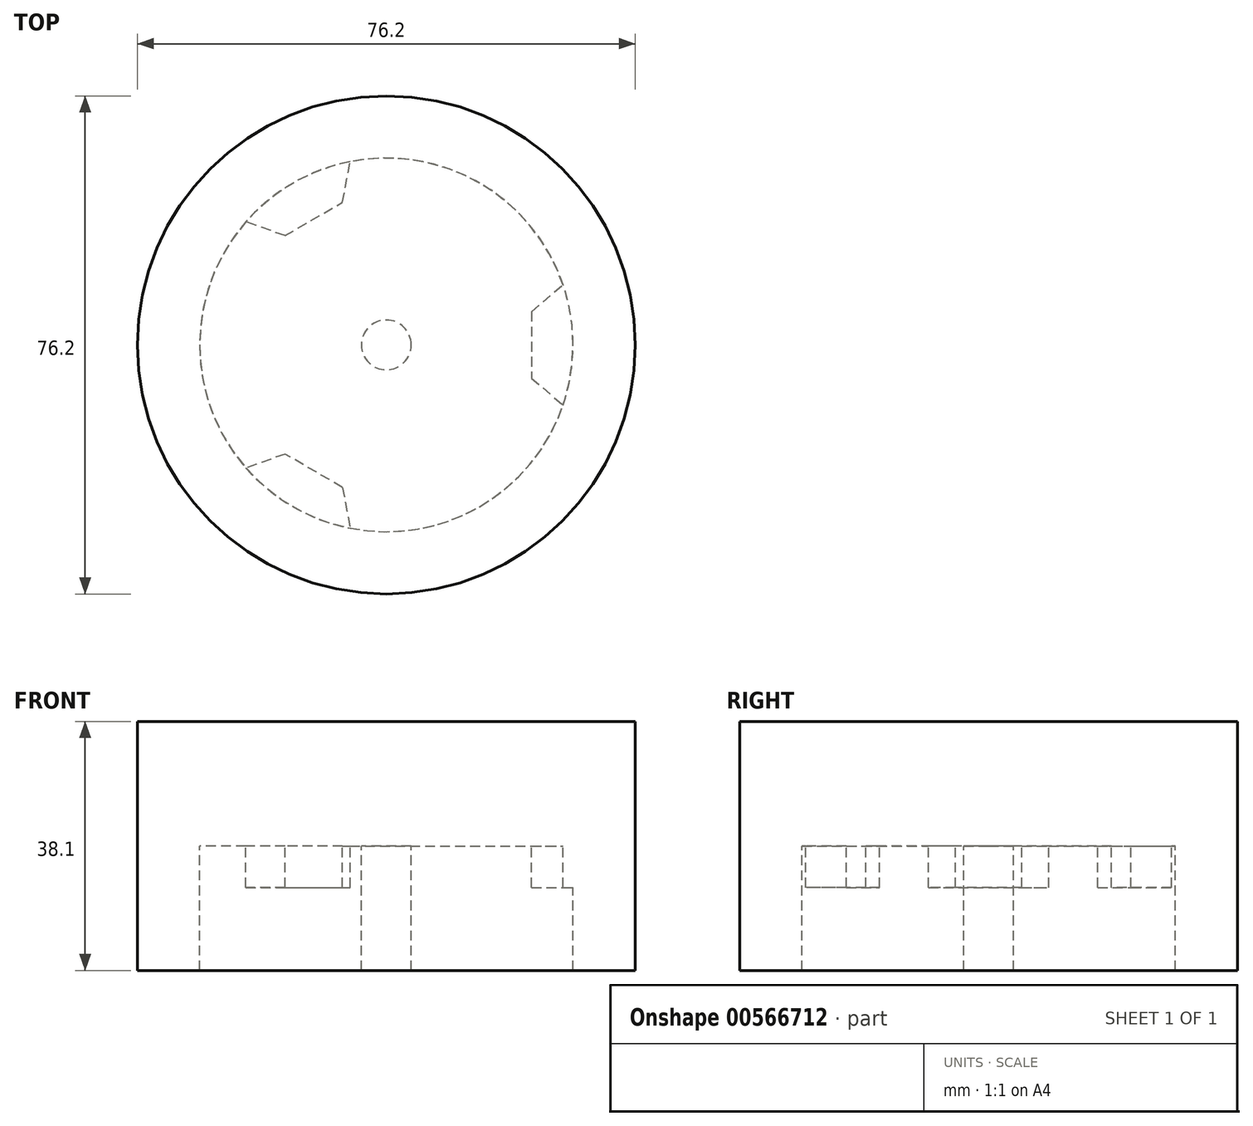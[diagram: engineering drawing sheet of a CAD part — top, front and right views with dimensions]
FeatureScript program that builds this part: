
annotation { "Feature Type Name" : "Feature", "Feature Type Description" : "" }
export const myFeature = defineFeature(function(context is Context, id is Id, definition is map)
    precondition{}
    {
        {
            var Q0;
            Q0=qCreatedBy(makeId("Front.planeOp"),FACE);
            var sketch = newSketch(context, id + "F0", { "sketchPlane" : qUnion([Q0])});
            skLineSegment(sketch, "E0", {"start": v(0, 0) * mm, "end": v(28.58, 0) * mm});
            skLineSegment(sketch, "E1", {"start": v(28.58, 0) * mm, "end": v(28.58, -19.05) * mm});
            skLineSegment(sketch, "E2", {"start": v(28.58, -19.05) * mm, "end": v(38.1, -19.05) * mm});
            skLineSegment(sketch, "E3", {"start": v(38.1, -19.05) * mm, "end": v(38.1, 19.05) * mm});
            skLineSegment(sketch, "E4", {"start": v(38.1, 19.05) * mm, "end": v(0, 19.05) * mm});
            skLineSegment(sketch, "E5", {"start": v(0, 19.05) * mm, "end": v(0, 0) * mm});
            skLineSegment(sketch, "E6", {"start": v(0, 0) * mm, "end": v(0, -19.05) * mm});
            skLineSegment(sketch, "E7", {"start": v(0, -19.05) * mm, "end": v(3.81, -19.05) * mm});
            skLineSegment(sketch, "E8", {"start": v(3.81, -19.05) * mm, "end": v(3.81, 0) * mm});
            skSolve(sketch);
        }
        {
            var Q0;
            Q0 = qSketchRegion(id + "F0", true);
            var Q1;
            Q1=sQuery(id+"F0.wireOp",EDGE,"E5");
            revolve(context, id + "F1", {"entities" : qUnion([Q0]), "axis" : qUnion([Q1]), "revolveType" : RevolveType.FULL});
        }
        {
            var Q0;
            Q0=makeQuery(id+"F1.opRevolve","SWEPT_FACE",FACE,{"disambiguationData":[OSD([sQuery(id+"F0.wireOp",EDGE,"E0")])]});
            var sketch = newSketch(context, id + "F2", { "sketchPlane" : qUnion([Q0])});
            skLineSegment(sketch, "E9", {"start": v(28.58, 0) * mm, "end": v(22.23, 0) * mm});
            skLineSegment(sketch, "E10", {"start": v(22.23, 0) * mm, "end": v(22.23, 5.08) * mm});
            skLineSegment(sketch, "E11", {"start": v(22.23, 5.08) * mm, "end": v(27.05, 9.2) * mm});
            skLineSegment(sketch, "E12", {"start": v(22.23, 0) * mm, "end": v(22.23, -5.08) * mm});
            skLineSegment(sketch, "E13", {"start": v(22.23, -5.08) * mm, "end": v(27.05, -9.2) * mm});
            skLineSegment(sketch, "E14.1.0", {"start": v(-11.11, -19.25) * mm, "end": v(-6.71, -21.79) * mm});
            skLineSegment(sketch, "E14.1.1", {"start": v(-11.11, -19.25) * mm, "end": v(-15.51, -16.7) * mm});
            skLineSegment(sketch, "E14.1.2", {"start": v(-6.71, -21.79) * mm, "end": v(-5.55, -28.03) * mm});
            skLineSegment(sketch, "E14.1.3", {"start": v(-15.51, -16.7) * mm, "end": v(-21.5, -18.82) * mm});
            skLineSegment(sketch, "E14.2.0", {"start": v(-11.11, 19.25) * mm, "end": v(-15.51, 16.7) * mm});
            skLineSegment(sketch, "E14.2.1", {"start": v(-11.11, 19.25) * mm, "end": v(-6.71, 21.79) * mm});
            skLineSegment(sketch, "E14.2.2", {"start": v(-15.51, 16.7) * mm, "end": v(-21.5, 18.82) * mm});
            skLineSegment(sketch, "E14.2.3", {"start": v(-6.71, 21.79) * mm, "end": v(-5.55, 28.03) * mm});
            skPoint(sketch, "E14.center", {"position": v(0, 0) * mm});
            skLineSegment(sketch, "E14.anchor1", {"start": v(0, 0) * mm, "end": v(22.23, 0) * mm, "construction": true});
            skLineSegment(sketch, "E14.anchor2", {"start": v(0, 0) * mm, "end": v(-11.11, 19.25) * mm, "construction": true});
            skLineSegment(sketch, "E15.1.4", {"start": v(0, 0) * mm, "end": v(-11.11, -19.25) * mm, "construction": true});
            skSolve(sketch);
        }
        {
            var Q0;
            Q0=makeQuery(id+"F2.imprint","IMPRINT",FACE,{"disambiguationData":[TD([[makeQuery(id+"F2.imprint","IMPRINT",EDGE,{"derivedFrom":sQuery(id+"F2.wireOp",EDGE,"E14.2.0")}),-1.0]])]});
            var Q1;
            {var subQ0=sQuery(id+"F2.wireOp",EDGE,"E9");Q1=makeQuery(id+"F2.imprint","IMPRINT",FACE,{"disambiguationData":[TD([[makeQuery(id+"F2.imprint","IMPRINT",EDGE,{"derivedFrom":subQ0}),-1.0]])]});}
            var Q2;
            {var subQ0=sQuery(id+"F2.wireOp",EDGE,"E9");Q2=makeQuery(id+"F2.imprint","IMPRINT",FACE,{"disambiguationData":[TD([[makeQuery(id+"F2.imprint","IMPRINT",EDGE,{"derivedFrom":subQ0}),1.0]])]});}
            var Q3;
            Q3=makeQuery(id+"F2.imprint","IMPRINT",FACE,{"disambiguationData":[TD([[makeQuery(id+"F2.imprint","IMPRINT",EDGE,{"derivedFrom":sQuery(id+"F2.wireOp",EDGE,"E14.1.0")}),-1.0]])]});
            extrude(context, id + "F3", {"entities" : qUnion([Q0, Q1, Q2, Q3]), "operationType" : NewBodyOperationType.ADD, "depth" : 6.35 * mm, "offsetDistance" : 25.4 * mm});
        }
    });
